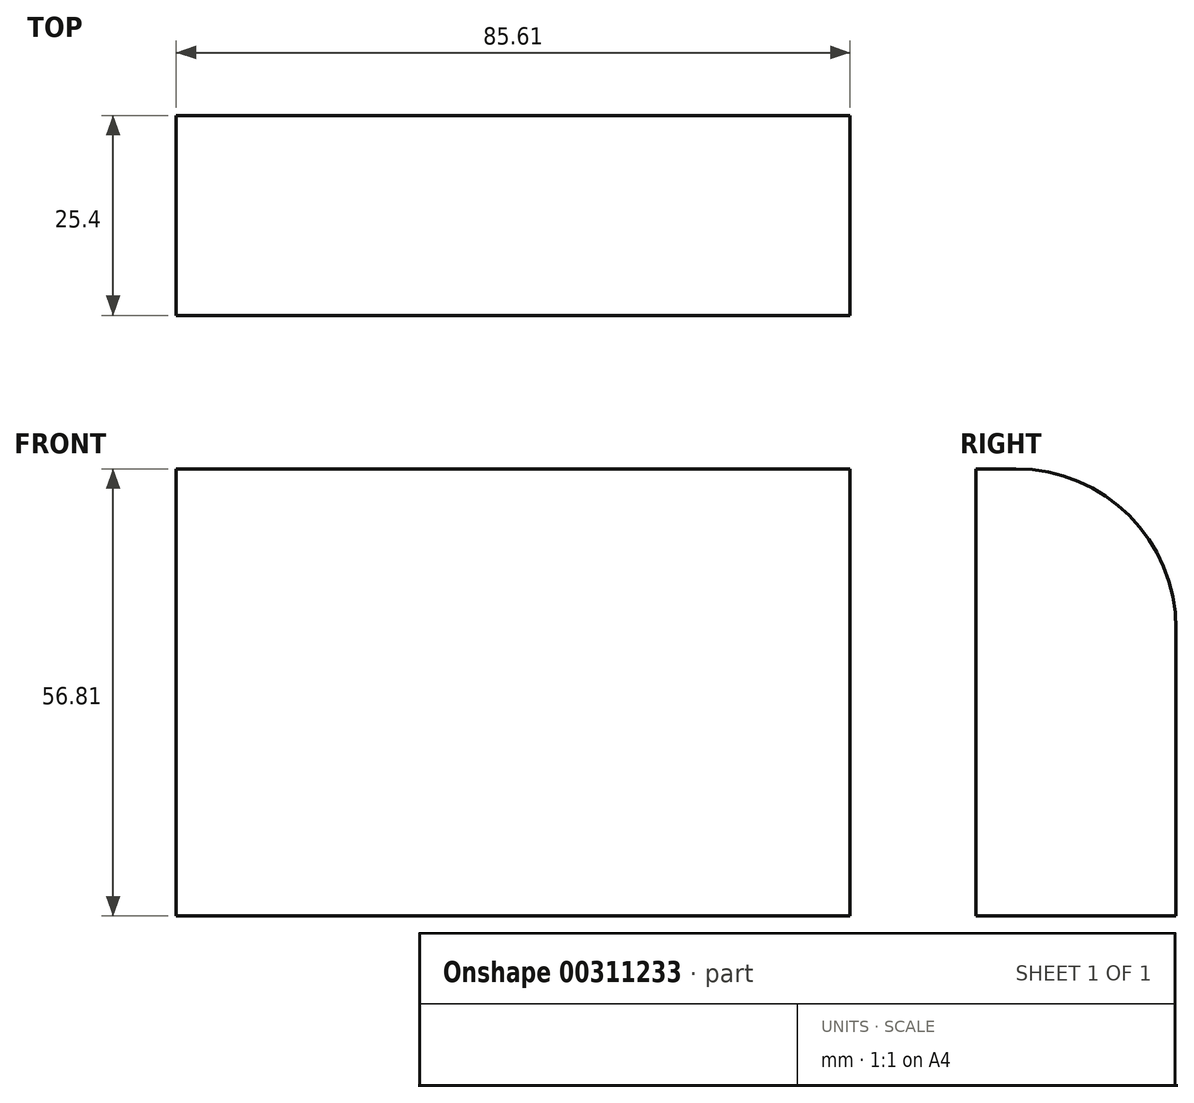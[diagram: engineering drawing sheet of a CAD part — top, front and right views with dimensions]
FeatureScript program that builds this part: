
annotation { "Feature Type Name" : "Feature", "Feature Type Description" : "" }
export const myFeature = defineFeature(function(context is Context, id is Id, definition is map)
    precondition{}
    {
        {
            var Q0;
            Q0=qCreatedBy(makeId("Front.planeOp"),FACE);
            var sketch = newSketch(context, id + "F0", { "sketchPlane" : qUnion([Q0])});
            skLineSegment(sketch, "E0.bottom", {"start": v(-41.9, 0) * mm, "end": v(43.7, 0) * mm});
            skLineSegment(sketch, "E0.top", {"start": v(-41.9, 56.81) * mm, "end": v(43.7, 56.81) * mm});
            skLineSegment(sketch, "E0.left", {"start": v(-41.9, 0) * mm, "end": v(-41.9, 56.81) * mm});
            skLineSegment(sketch, "E0.right", {"start": v(43.7, 0) * mm, "end": v(43.7, 56.81) * mm});
            skSolve(sketch);
        }
        {
            var Q0;
            Q0=makeQuery(id+"F0.imprint","IMPRINT",FACE,{"disambiguationData":[TD([[makeQuery(id+"F0.imprint","IMPRINT",EDGE,{"derivedFrom":sQuery(id+"F0.wireOp",EDGE,"E0.bottom")}),1.0]])]});
            extrude(context, id + "F1", {"entities" : qUnion([Q0]), "depth" : 25.4 * mm});
        }
        {
            var Q0;
            Q0=makeQuery(id+"F1.opExtrude","CAP_EDGE",EDGE,{"disambiguationData":[OSD([sQuery(id+"F0.wireOp",EDGE,"E0.top")])],"isStart":true});
            fillet(context, id + "F2", {"entities" : qUnion([Q0]), "radius" : 20.32 * mm, "tangentPropagation" : true, "allowEdgeOverflow" : false});
        }
        {
            var Q0;
            Q0=makeQuery(id+"F1.opExtrude","CAP_FACE",FACE,{"disambiguationData":[OSD([sQuery(id+"F0.wireOp",EDGE,"E0.bottom"),sQuery(id+"F0.wireOp",EDGE,"E0.top"),sQuery(id+"F0.wireOp",EDGE,"E0.left"),sQuery(id+"F0.wireOp",EDGE,"E0.right")])],"isStart":true});
            var sketch = newSketch(context, id + "F3", { "sketchPlane" : qUnion([Q0])});
            skSolve(sketch);
        }
    });
